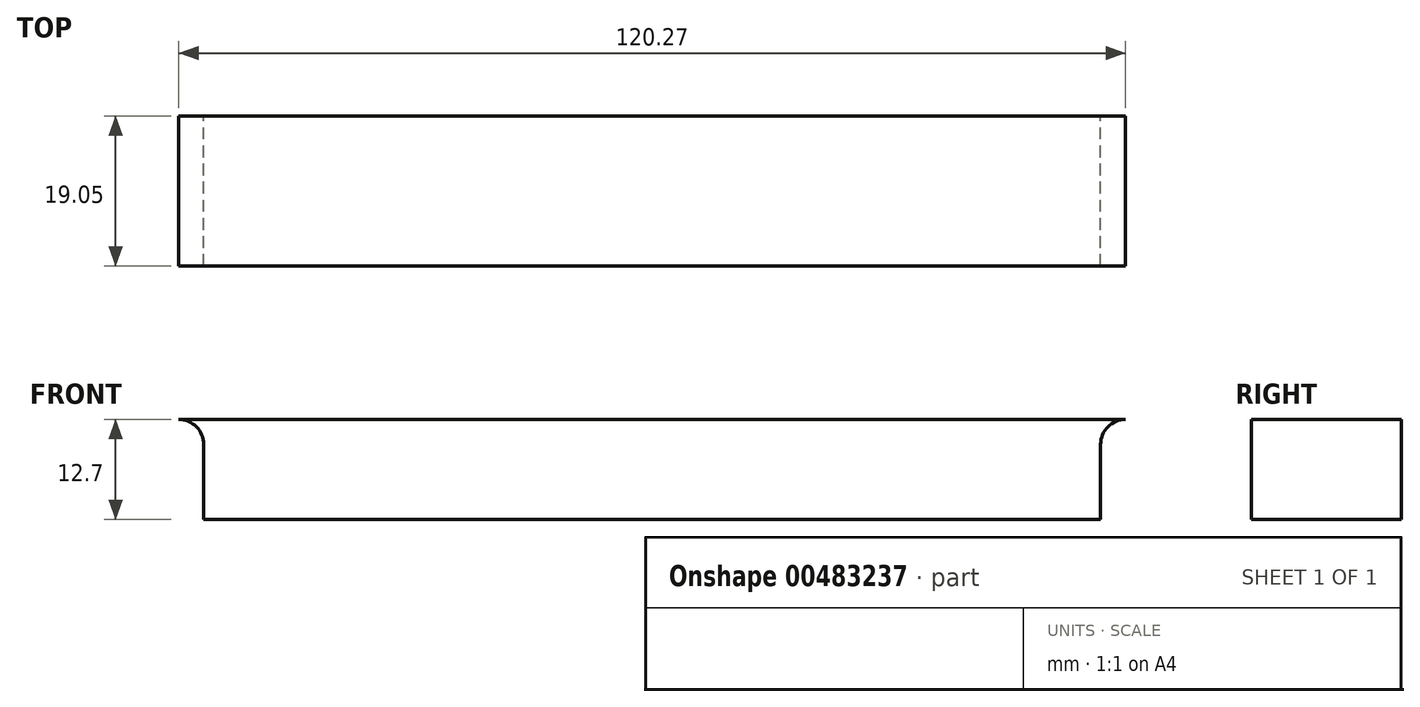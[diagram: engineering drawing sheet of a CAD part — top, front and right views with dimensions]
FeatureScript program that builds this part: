
annotation { "Feature Type Name" : "Feature", "Feature Type Description" : "" }
export const myFeature = defineFeature(function(context is Context, id is Id, definition is map)
    precondition{}
    {
        {
            var Q0;
            Q0=qCreatedBy(makeId("Front.planeOp"),FACE);
            var sketch = newSketch(context, id + "F0", { "sketchPlane" : qUnion([Q0])});
            skLineSegment(sketch, "E0.bottom", {"start": v(118.56, 6.35) * mm, "end": v(-1.71, 6.35) * mm});
            skLineSegment(sketch, "E0.top", {"start": v(115.39, -6.35) * mm, "end": v(1.46, -6.35) * mm});
            skPoint(sketch, "E0.middle", {"position": v(0, 0) * mm});
            skLineSegment(sketch, "E1", {"start": v(1.46, 3.18) * mm, "end": v(1.46, -6.35) * mm});
            skLineSegment(sketch, "E2", {"start": v(115.39, 3.17) * mm, "end": v(115.39, -6.35) * mm});
            skArc(sketch, "E3", {"start": v(118.56, 6.35) * mm, "mid": v(116.32, 5.42) * mm, "end": v(115.39, 3.17) * mm});
            skPoint(sketch, "E4.orphan", {"position": v(1.71, -6.35) * mm});
            skArc(sketch, "E5", {"start": v(1.46, 3.18) * mm, "mid": v(0.53, 5.42) * mm, "end": v(-1.71, 6.35) * mm});
            skPoint(sketch, "E6.orphan", {"position": v(-118.56, -6.35) * mm});
            skSolve(sketch);
        }
        {
            var Q0;
            Q0=qSketchRegion(id+"F0",true);
            extrude(context, id + "F1", {"entities" : qUnion([Q0]), "depth" : 19.05 * mm});
        }
    });
